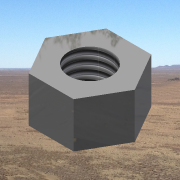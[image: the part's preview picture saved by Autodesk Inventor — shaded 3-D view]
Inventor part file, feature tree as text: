
AUTODESK INVENTOR PART (.ipt)
format: ipt  version: 2013 SP2 (Build 170200200, 200)  size: 129,024 bytes
history: native  units: in
note: dims shown in document units (in); Inventor stores cm internally (conversion verified against a paired STEP export)
features: sketch x2, extrude x1, hole x1
ambient origin geometry x8: Origin, YZ Plane, XZ Plane, XY Plane, X Axis, Y Axis, Z Axis, Center Point
bodies: Solid1 (feature_tree)
feature tree (4):
  extrude  "Extrusion1"  Depth=0.3281in TaperAngle=0.0deg
  hole  "Hole1"  [1 undecoded]
  sketch  "Sketch1"  dims[d0=0.5625in d1=0.3281in d2=0.0in]
  sketch  "Sketch2"  dims[d3=0.375in d5=0.307in d6=0.75in d7=0.375in d8=0.25in d9=0.5635in d10=1.0in d11=0.8108in]
note: 1 required parameter value undecoded (feature->parameter linkage not recoverable at this tier; creation-order binding heuristic only, values carry confidence <= 0.55)
